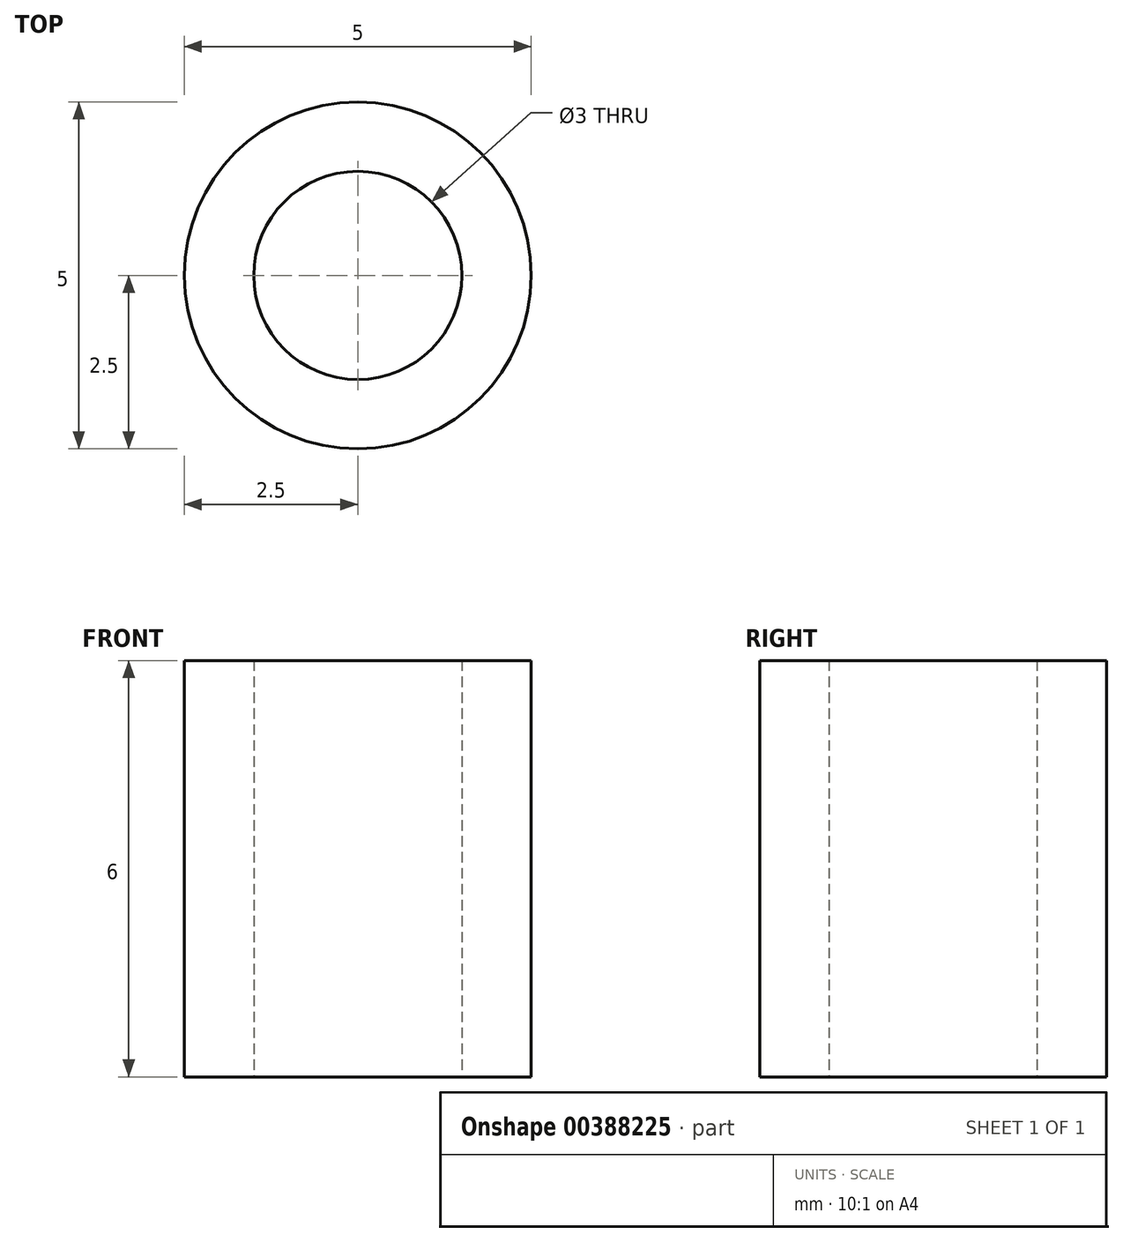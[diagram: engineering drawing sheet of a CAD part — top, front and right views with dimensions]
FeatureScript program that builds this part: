
annotation { "Feature Type Name" : "Feature", "Feature Type Description" : "" }
export const myFeature = defineFeature(function(context is Context, id is Id, definition is map)
    precondition{}
    {
        {
            var Q0;
            Q0=qCreatedBy(makeId("Top.planeOp"),FACE);
            var sketch = newSketch(context, id + "F0", { "sketchPlane" : qUnion([Q0])});
            skCircle(sketch, "E0", {"center": v(0, 0) * mm, "radius": 2.5 * mm});
            skCircle(sketch, "E1", {"center": v(0, 0) * mm, "radius": 1.5 * mm});
            skSolve(sketch);
        }
        {
            var Q0;
            Q0=makeQuery(id+"F0.imprint","IMPRINT",FACE,{"disambiguationData":[TD([[makeQuery(id+"F0.imprint","IMPRINT",EDGE,{"derivedFrom":sQuery(id+"F0.wireOp",EDGE,"E0")}),1.0]])]});
            extrude(context, id + "F1", {"entities" : qUnion([Q0]), "depth" : 6 * mm});
        }
    });
